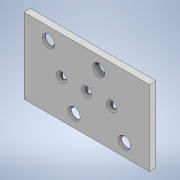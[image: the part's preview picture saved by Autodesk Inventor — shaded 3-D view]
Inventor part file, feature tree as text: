
AUTODESK INVENTOR PART (.ipt)
format: ipt  version: 2021 (Build 250183000, 183)  size: 527,872 bytes
history: native  units: in
note: dims shown in document units (in); Inventor stores cm internally (conversion verified against a paired STEP export)
features: projected_geometry x9, extrude x7, sketch x7, chamfer x2, pattern_linear x2
ambient origin geometry x8: Origin, YZ Plane, XZ Plane, XY Plane, X Axis, Y Axis, Z Axis, Center Point
bodies: Solid1 (feature_tree)
feature tree (27):
  extrude  "Extrusion1"  Depth=0.15in
  extrude  "Extrusion2"  Depth=0.239in
  extrude  "Extrusion3"  Depth=0.0071in TaperAngle=0.0deg
  chamfer  "Chamfer1"  Distance=0.0746in
  extrude  "Extrusion4"  Depth=0.05in
  extrude  "Extrusion5"  TaperAngle=0.0deg  [1 undecoded]
  pattern_linear  "Rectangular Pattern1"  Spacing1=0.004in  [1 undecoded]
  extrude  "Extrusion6"  Depth=0.3937in
  pattern_linear  "Rectangular Pattern2"  Spacing1=0.002in  [1 undecoded]
  chamfer  "Chamfer2"  Distance=0.0071in
  extrude  "Extrusion7"  Depth=0.3937in
  sketch  "Sketch1"  dims[d0=0.25in d1=0.15in]
  sketch  "Sketch2"  dims[d2=0.0059in d3=0.0in d4=0.239in]
  projected_geometry  "Projected Loop1"
  sketch  "Sketch3"  dims[d5=0.139in d6=0.0071in d7=0.0in]
  projected_geometry  "Projected Loop2"
  sketch  "Sketch4"  dims[d8=0.01in]
  sketch  "Sketch5"  dims[d9=0.0335in]
  projected_geometry  "Projected Loop3"
  sketch  "Sketch6"  dims[d10=0.7874in d12=0.0315in d13=0.3937in d15=1.0in]
  projected_geometry  "Projected Loop4"
  projected_geometry  "Projected Loop5"
  sketch  "Sketch7"  dims[d17=0.012in d18=0.0746in d19=1.1811in d21=0.05in d22=0.3937in d24=1.0in d26=0.0in d27=0.0in d28=0.004in d29=0.125in d30=45.0deg d31=0.002in d32=0.002in d33=0.0071in d34=0.0in d35=0.0236in d36=0.05in d37=0.05in d38=0.0in d39=0.0in d40=0.7874in d42=0.1in d43=0.7874in d45=0.076in d46=0.3937in d48=1.0in d52=0.01in d54=0.0565in d55=0.0071in d56=0.0in d57=1.1811in d59=0.05in d60=0.007in d61=0.125in d62=45.0deg d63=0.024in d64=0.7874in d66=0.1in d67=0.3937in d69=1.0in d71=0.0in d72=0.0in]
  projected_geometry  "Projected Loop6"
  projected_geometry  "Projected Loop7"
  projected_geometry  "Projected Loop8"
  projected_geometry  "Projected Loop9"
note: 3 required parameter values undecoded (feature->parameter linkage not recoverable at this tier; creation-order binding heuristic only, values carry confidence <= 0.55)
